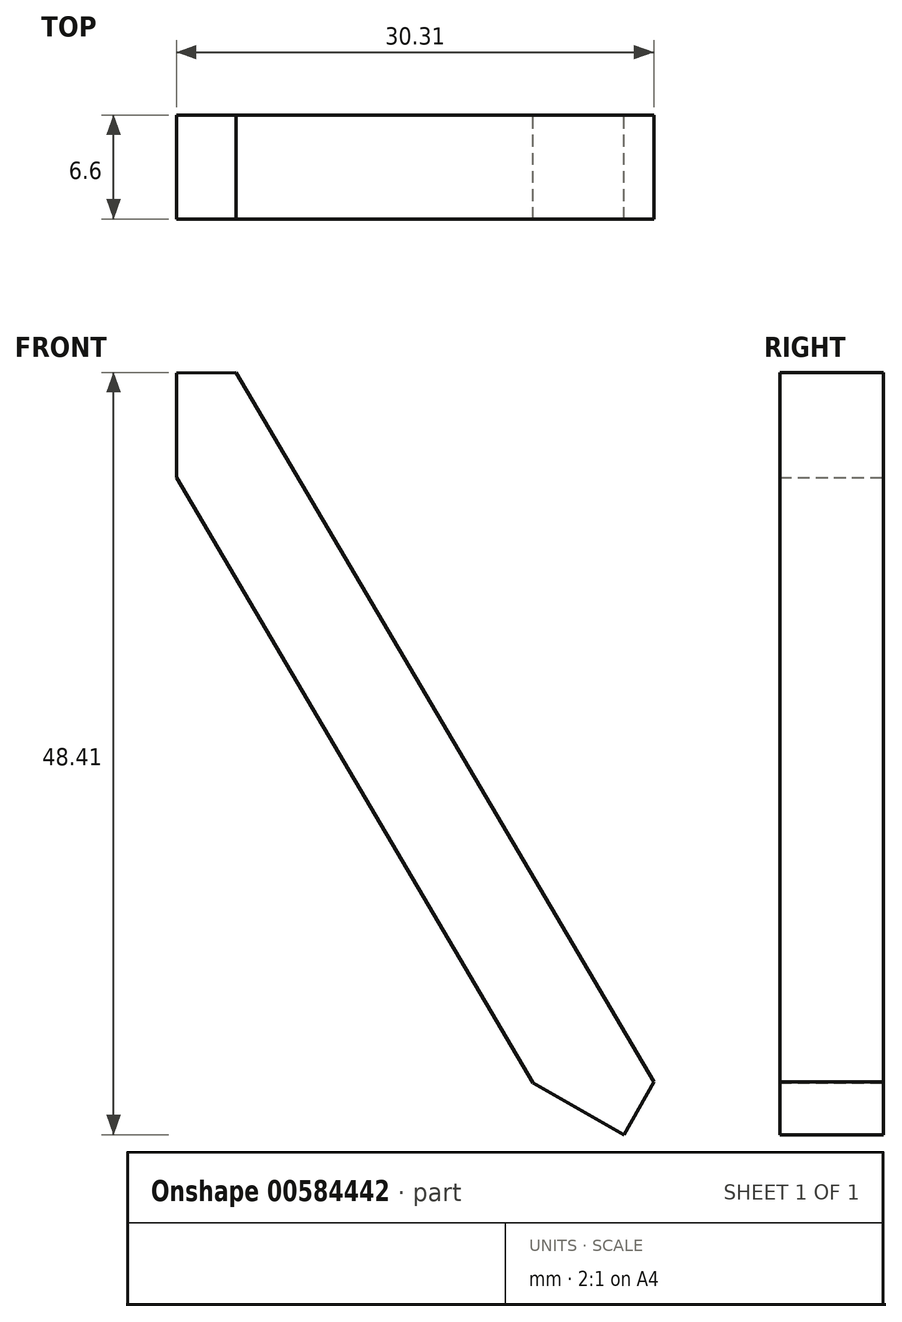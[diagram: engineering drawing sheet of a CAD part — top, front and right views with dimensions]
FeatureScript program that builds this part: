
annotation { "Feature Type Name" : "Feature", "Feature Type Description" : "" }
export const myFeature = defineFeature(function(context is Context, id is Id, definition is map)
    precondition{}
    {
        {
            var Q0;
            Q0=qCreatedBy(makeId("Front.planeOp"),FACE);
            var sketch = newSketch(context, id + "F0", { "sketchPlane" : qUnion([Q0])});
            skLineSegment(sketch, "E0", {"start": v(-24.6, 37.2) * mm, "end": v(-1.98, -1.25) * mm});
            skLineSegment(sketch, "E1.2", {"start": v(-20.83, 43.88) * mm, "end": v(5.7, -1.19) * mm});
            skLineSegment(sketch, "E2", {"start": v(-24.6, 37.2) * mm, "end": v(-20.83, 43.88) * mm});
            skLineSegment(sketch, "E3", {"start": v(-1.98, -1.25) * mm, "end": v(5.7, -1.19) * mm});
            skLineSegment(sketch, "E4", {"start": v(-24.67, 43.85) * mm, "end": v(-20.83, 43.88) * mm});
            skLineSegment(sketch, "E5", {"start": v(5.7, -1.19) * mm, "end": v(3.8, -4.53) * mm});
            skLineSegment(sketch, "E6", {"start": v(-1.98, -1.25) * mm, "end": v(3.86, -4.56) * mm});
            skPoint(sketch, "E6.endSnap0", {"position": v(-0.03, -4.56) * mm});
            skLineSegment(sketch, "E7", {"start": v(-24.6, 37.2) * mm, "end": v(-24.6, 43.85) * mm});
            skPoint(sketch, "E7.endSnap0", {"position": v(-24.67, 43.85) * mm});
            skPoint(sketch, "E1.0.end.orphan", {"position": v(-28.5, 43.81) * mm});
            skPoint(sketch, "E8.orphan", {"position": v(1.92, -7.87) * mm});
            skLineSegment(sketch, "E9", {"start": v(-20.83, 43.88) * mm, "end": v(-24.6, 43.85) * mm});
            skSolve(sketch);
        }
        {
            var Q0;
            Q0 = qSketchRegion(id + "F0", true);
            extrude(context, id + "F1", {"entities" : qUnion([Q0]), "depth" : 6.6 * mm, "offsetDistance" : 25 * mm});
        }
    });
